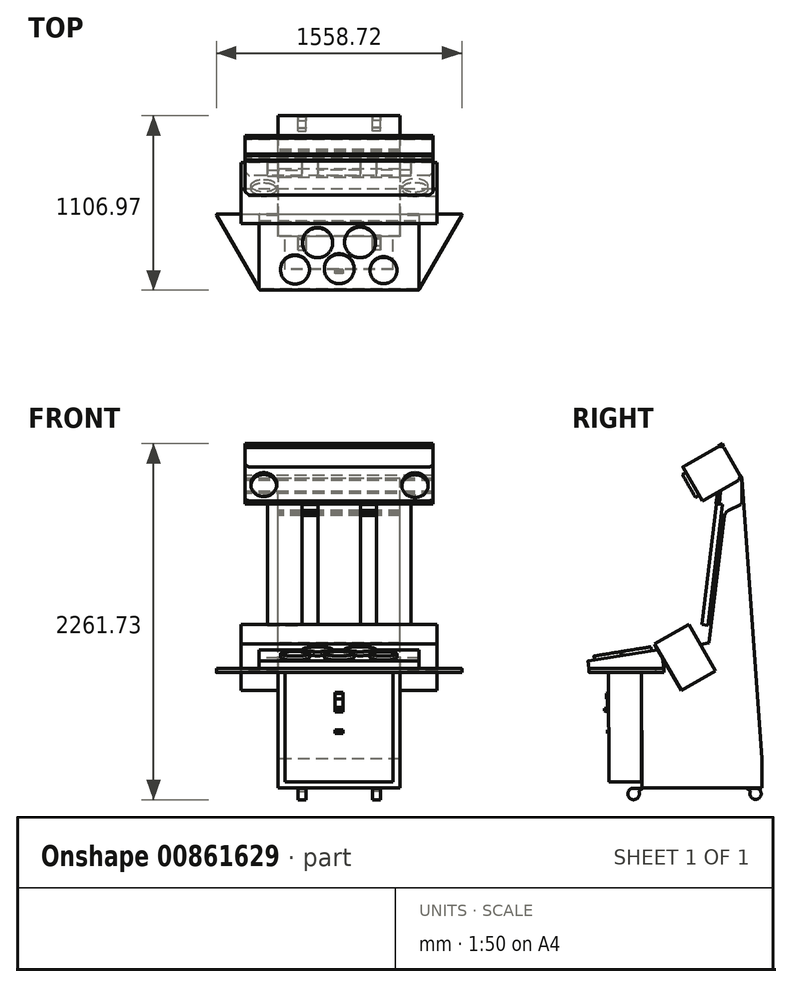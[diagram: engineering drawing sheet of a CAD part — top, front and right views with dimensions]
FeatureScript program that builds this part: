
annotation { "Feature Type Name" : "Feature", "Feature Type Description" : "" }
export const myFeature = defineFeature(function(context is Context, id is Id, definition is map)
    precondition{}
    {
        {
            var Q0;
            Q0=qCreatedBy(makeId("Right.planeOp"),FACE);
            cPlane(context, id + "F0", {"entities" : qUnion([Q0]), "cplaneType" : CPlaneType.OFFSET, "offset" : 210 * mm, "width" : 152.4 * mm, "height" : 152.4 * mm});
        }
        {
            var Q0;
            Q0=qCreatedBy(makeId("Right.planeOp"),FACE);
            var sketch = newSketch(context, id + "F1", { "sketchPlane" : qUnion([Q0])});
            skLineSegment(sketch, "E0", {"start": v(135.82, -1032.26) * mm, "end": v(135.82, 1003.74) * mm});
            skLineSegment(sketch, "E1", {"start": v(-110.75, -958.44) * mm, "end": v(-873.39, -958.44) * mm});
            skLineSegment(sketch, "E2", {"start": v(-873.39, -931.24) * mm, "end": v(-111.51, -931.24) * mm});
            skLineSegment(sketch, "E3", {"start": v(-110.75, -958.44) * mm, "end": v(-110.75, -776.07) * mm});
            skLineSegment(sketch, "E4", {"start": v(-110.75, -776.07) * mm, "end": v(-237.96, 1006.21) * mm});
            skLineSegment(sketch, "E5", {"start": v(-873.39, -958.44) * mm, "end": v(-877.45, -225.16) * mm});
            skLineSegment(sketch, "E6", {"start": v(-877.45, -225.16) * mm, "end": v(-784.62, -224.64) * mm});
            skLineSegment(sketch, "E7", {"start": v(-784.62, -224.64) * mm, "end": v(-803.14, -88.35) * mm});
            skLineSegment(sketch, "E8", {"start": v(-803.14, -88.35) * mm, "end": v(-449.35, -40.28) * mm});
            skLineSegment(sketch, "E9", {"start": v(-449.35, -40.28) * mm, "end": v(-351.09, 769.66) * mm});
            skLineSegment(sketch, "E10", {"start": v(-351.09, 769.66) * mm, "end": v(-345.66, 781.97) * mm});
            skLineSegment(sketch, "E11", {"start": v(-345.66, 781.97) * mm, "end": v(-337.87, 793.88) * mm});
            skLineSegment(sketch, "E12", {"start": v(-337.87, 793.88) * mm, "end": v(-325.04, 803.04) * mm});
            skLineSegment(sketch, "E13", {"start": v(-325.04, 803.04) * mm, "end": v(-246.25, 841.07) * mm});
            skLineSegment(sketch, "E14", {"start": v(-246.25, 841.07) * mm, "end": v(-242.89, 847.1) * mm});
            skLineSegment(sketch, "E15", {"start": v(-242.89, 847.1) * mm, "end": v(-239.22, 854.43) * mm});
            skLineSegment(sketch, "E16", {"start": v(-239.22, 854.43) * mm, "end": v(-237.96, 1006.21) * mm});
            skSolve(sketch);
        }
        {
            var Q0;
            Q0=makeQuery(id+"F1.imprint","IMPRINT",FACE,{"disambiguationData":[TD([[makeQuery(id+"F1.imprint","IMPRINT",EDGE,{"derivedFrom":sQuery(id+"F1.wireOp",EDGE,"E1")}),-1.0]])]});
            extrude(context, id + "F2", {"entities" : qUnion([Q0]), "depth" : 774.7 * mm, "offsetDistance" : 25.4 * mm, "symmetric" : true});
        }
        {
            var Q0;
            Q0=qCreatedBy(makeId("Right.planeOp"),FACE);
            var sketch = newSketch(context, id + "F3", { "sketchPlane" : qUnion([Q0])});
            skLineSegment(sketch, "E17", {"start": v(-615.4, 1079.1) * mm, "end": v(-490.16, 861.86) * mm});
            skLineSegment(sketch, "E18", {"start": v(-490.16, 861.86) * mm, "end": v(-262.73, 992.99) * mm});
            skLineSegment(sketch, "E19", {"start": v(-262.73, 992.99) * mm, "end": v(-255.5, 1005.4) * mm});
            skLineSegment(sketch, "E20", {"start": v(-255.5, 1005.4) * mm, "end": v(-252.31, 1026.09) * mm});
            skLineSegment(sketch, "E21", {"start": v(-252.31, 1026.09) * mm, "end": v(-354.74, 1202.65) * mm});
            skLineSegment(sketch, "E22", {"start": v(-354.74, 1202.65) * mm, "end": v(-367.56, 1207.47) * mm});
            skLineSegment(sketch, "E23", {"start": v(-367.56, 1207.47) * mm, "end": v(-382.08, 1207.47) * mm});
            skLineSegment(sketch, "E24", {"start": v(-382.08, 1207.47) * mm, "end": v(-396.8, 1202.65) * mm});
            skLineSegment(sketch, "E25", {"start": v(-396.8, 1202.65) * mm, "end": v(-615.4, 1079.1) * mm});
            skLineSegment(sketch, "E26", {"start": v(-538.42, 1122.61) * mm, "end": v(-413.55, 906.03) * mm});
            skSolve(sketch);
        }
        {
            var Q0;
            Q0 = qSketchRegion(id + "F3", true);
            extrude(context, id + "F4", {"entities" : qUnion([Q0]), "depth" : 1193.8 * mm, "offsetDistance" : 25.4 * mm, "symmetric" : true});
        }
        {
            var Q0;
            Q0=qCreatedBy(makeId("Right.planeOp"),FACE);
            var sketch = newSketch(context, id + "F5", { "sketchPlane" : qUnion([Q0])});
            skLineSegment(sketch, "E27", {"start": v(-795.55, -46.75) * mm, "end": v(-576.34, 79.37) * mm});
            skLineSegment(sketch, "E28", {"start": v(-576.34, 79.37) * mm, "end": v(-406.78, -215.33) * mm});
            skLineSegment(sketch, "E29", {"start": v(-406.78, -215.33) * mm, "end": v(-624.22, -340.43) * mm});
            skLineSegment(sketch, "E30", {"start": v(-624.22, -340.43) * mm, "end": v(-795.55, -46.75) * mm});
            skLineSegment(sketch, "E31", {"start": v(-749.98, -124.87) * mm, "end": v(-532, 2.3) * mm});
            skSolve(sketch);
        }
        {
            var Q0;
            Q0 = qSketchRegion(id + "F5", true);
            extrude(context, id + "F6", {"entities" : qUnion([Q0]), "operationType" : NewBodyOperationType.ADD, "depth" : 1244.6 * mm, "offsetDistance" : 25.4 * mm, "symmetric" : true});
        }
        {
            var Q0;
            Q0=qCreatedBy(makeId("Right.planeOp"),FACE);
            var sketch = newSketch(context, id + "F7", { "sketchPlane" : qUnion([Q0])});
            skLineSegment(sketch, "E32", {"start": v(-1223.23, -201.66) * mm, "end": v(-733.46, -201.66) * mm});
            skLineSegment(sketch, "E33", {"start": v(-733.46, -201.66) * mm, "end": v(-753.47, -78.71) * mm});
            skLineSegment(sketch, "E34", {"start": v(-753.47, -78.71) * mm, "end": v(-1229.15, -156.15) * mm});
            skLineSegment(sketch, "E35", {"start": v(-1217.72, -154.29) * mm, "end": v(-1210, -201.66) * mm});
            skLineSegment(sketch, "E36", {"start": v(-1141.93, -141.95) * mm, "end": v(-1132.2, -201.66) * mm});
            skSolve(sketch);
        }
        {
            var Q0;
            Q0 = qSketchRegion(id + "F7", true);
            extrude(context, id + "F8", {"entities" : qUnion([Q0]), "operationType" : NewBodyOperationType.ADD, "depth" : 1016 * mm, "offsetDistance" : 25.4 * mm, "symmetric" : true});
        }
        {
            var Q0;
            Q0=qCreatedBy(makeId("Right.planeOp"),FACE);
            var sketch = newSketch(context, id + "F9", { "sketchPlane" : qUnion([Q0])});
            skLineSegment(sketch, "E37", {"start": v(-977.2, -301.46) * mm, "end": v(-901, -301.46) * mm});
            skLineSegment(sketch, "E38", {"start": v(-977.2, -301.46) * mm, "end": v(-977.2, -851.46) * mm});
            skLineSegment(sketch, "E39", {"start": v(-977.2, -851.46) * mm, "end": v(-901.79, -851.46) * mm});
            skLineSegment(sketch, "E40", {"start": v(-901.79, -851.46) * mm, "end": v(-901, -301.46) * mm});
            skSolve(sketch);
        }
        {
            var Q0;
            Q0 = qSketchRegion(id + "F9", true);
            extrude(context, id + "F10", {"entities" : qUnion([Q0]), "depth" : 533.4 * mm, "offsetDistance" : 25.4 * mm, "symmetric" : true});
        }
        {
            var Q0;
            Q0=makeQuery(id+"F8.opExtrude","SWEPT_FACE",FACE,{"disambiguationData":[OSD([sQuery(id+"F7.wireOp",EDGE,"E34")])]});
            var sketch = newSketch(context, id + "F11", { "sketchPlane" : qUnion([Q0])});
            skCircle(sketch, "E41", {"center": v(-137.58, -918.6) * mm, "radius": 95.8 * mm});
            skCircle(sketch, "E42", {"center": v(132.62, -915.7) * mm, "radius": 98.49 * mm});
            skCircle(sketch, "E43", {"center": v(-280.8, -1092.1) * mm, "radius": 91.63 * mm});
            skCircle(sketch, "E44", {"center": v(281.26, -1096.57) * mm, "radius": 85.14 * mm});
            skCircle(sketch, "E45", {"center": v(0, -1086.83) * mm, "radius": 94.68 * mm});
            skSolve(sketch);
        }
        {
            var Q0;
            Q0 = qSketchRegion(id + "F11", true);
            extrude(context, id + "F12", {"entities" : qUnion([Q0]), "operationType" : NewBodyOperationType.ADD, "depth" : 50.8 * mm, "offsetDistance" : 25.4 * mm, "symmetric" : true});
        }
        {
            var Q0;
            Q0=qCreatedBy(id+"F0.planeOp",FACE);
            var sketch = newSketch(context, id + "F13", { "sketchPlane" : qUnion([Q0])});
            skLineSegment(sketch, "E46", {"start": v(-207.52, -962.58) * mm, "end": v(-154.05, -1009.27) * mm});
            skLineSegment(sketch, "E47", {"start": v(-207.52, -962.58) * mm, "end": v(-142.16, -962.58) * mm});
            skLineSegment(sketch, "E48", {"start": v(-142.16, -962.58) * mm, "end": v(-136.22, -992.3) * mm});
            skLineSegment(sketch, "E49", {"start": v(-136.22, -992.3) * mm, "end": v(-138.79, -1001.43) * mm});
            skLineSegment(sketch, "E50", {"start": v(-138.79, -1001.43) * mm, "end": v(-142.78, -1006) * mm});
            skLineSegment(sketch, "E51", {"start": v(-142.78, -1006) * mm, "end": v(-154.05, -1009.27) * mm});
            skArc(sketch, "E52", {"start": v(-185.18, -982.09) * mm, "mid": v(-137.8, -1029.41) * mm, "end": v(-142.16, -962.58) * mm});
            skLineSegment(sketch, "E53", {"start": v(-871.96, -962.48) * mm, "end": v(-937.74, -962.48) * mm});
            skLineSegment(sketch, "E54", {"start": v(-937.74, -962.48) * mm, "end": v(-945.38, -989.64) * mm});
            skLineSegment(sketch, "E55", {"start": v(-945.38, -989.64) * mm, "end": v(-944.06, -1001.7) * mm});
            skLineSegment(sketch, "E56", {"start": v(-944.06, -1001.7) * mm, "end": v(-936.38, -1007.05) * mm});
            skLineSegment(sketch, "E57", {"start": v(-936.38, -1007.05) * mm, "end": v(-924.96, -1007.05) * mm});
            skLineSegment(sketch, "E58", {"start": v(-924.96, -1007.05) * mm, "end": v(-871.96, -962.48) * mm});
            skArc(sketch, "E59", {"start": v(-937.74, -962.48) * mm, "mid": v(-941.48, -1031.6) * mm, "end": v(-894.12, -981.11) * mm});
            skSolve(sketch);
        }
        {
            var Q0;
            Q0 = qSketchRegion(id + "F13", true);
            extrude(context, id + "F14", {"entities" : qUnion([Q0]), "depth" : 50.8 * mm, "offsetDistance" : 25.4 * mm});
        }
        {
            var Q0;
            Q0=qCreatedBy(makeId("Right.planeOp"),FACE);
            var sketch = newSketch(context, id + "F15", { "sketchPlane" : qUnion([Q0])});
            skLineSegment(sketch, "E60", {"start": v(-362.5, 840.95) * mm, "end": v(-401.41, 843.95) * mm});
            skLineSegment(sketch, "E61", {"start": v(-401.41, 843.95) * mm, "end": v(-493.98, 77.86) * mm});
            skLineSegment(sketch, "E62", {"start": v(-493.98, 77.86) * mm, "end": v(-454.6, 73.1) * mm});
            skLineSegment(sketch, "E63", {"start": v(-454.6, 73.1) * mm, "end": v(-362.5, 840.95) * mm});
            skSolve(sketch);
        }
        {
            var Q0;
            Q0 = qSketchRegion(id + "F15", true);
            extrude(context, id + "F16", {"entities" : qUnion([Q0]), "depth" : 270 * mm, "offsetDistance" : 25.4 * mm, "symmetric" : true});
        }
        {
            var Q0;
            Q0=qCreatedBy(makeId("Right.planeOp"),FACE);
            var sketch = newSketch(context, id + "F17", { "sketchPlane" : qUnion([Q0])});
            skLineSegment(sketch, "E64", {"start": v(-255.02, 994.86) * mm, "end": v(-236.35, 1006.75) * mm});
            skLineSegment(sketch, "E65", {"start": v(-255.02, 994.86) * mm, "end": v(-249.98, 1026.27) * mm});
            skLineSegment(sketch, "E66", {"start": v(-249.98, 1026.27) * mm, "end": v(-236.35, 1006.75) * mm});
            skLineSegment(sketch, "E67", {"start": v(-364.5, 1227.17) * mm, "end": v(-391.26, 1211.27) * mm});
            skLineSegment(sketch, "E68", {"start": v(-391.26, 1211.27) * mm, "end": v(-355.17, 1209) * mm});
            skLineSegment(sketch, "E69", {"start": v(-355.17, 1209) * mm, "end": v(-364.5, 1227.17) * mm});
            skLineSegment(sketch, "E70", {"start": v(-403.29, 847.41) * mm, "end": v(-395.65, 911.5) * mm});
            skLineSegment(sketch, "E71", {"start": v(-395.65, 911.5) * mm, "end": v(-375.7, 924.23) * mm});
            skLineSegment(sketch, "E72", {"start": v(-403.29, 847.41) * mm, "end": v(-362.3, 842.52) * mm});
            skLineSegment(sketch, "E73", {"start": v(-375.7, 924.23) * mm, "end": v(-382.8, 844.97) * mm});
            skLineSegment(sketch, "E74", {"start": v(-373.82, 743.38) * mm, "end": v(-375.43, 737.85) * mm});
            skLineSegment(sketch, "E75", {"start": v(-375.43, 737.85) * mm, "end": v(-355.09, 737.85) * mm});
            skLineSegment(sketch, "E76", {"start": v(-355.09, 737.85) * mm, "end": v(-355.09, 741.95) * mm});
            skLineSegment(sketch, "E77", {"start": v(-355.09, 741.95) * mm, "end": v(-373.82, 743.38) * mm});
            skLineSegment(sketch, "E78", {"start": v(-388.1, 623.82) * mm, "end": v(-369, 622.22) * mm});
            skLineSegment(sketch, "E79", {"start": v(-369, 622.22) * mm, "end": v(-369.41, 617.36) * mm});
            skLineSegment(sketch, "E80", {"start": v(-369.41, 617.36) * mm, "end": v(-388.83, 619) * mm});
            skLineSegment(sketch, "E81", {"start": v(-388.83, 619) * mm, "end": v(-388.1, 623.82) * mm});
            skLineSegment(sketch, "E82", {"start": v(-405.23, 483.75) * mm, "end": v(-386.14, 483.75) * mm});
            skLineSegment(sketch, "E83", {"start": v(-386.14, 483.75) * mm, "end": v(-386.65, 477.65) * mm});
            skLineSegment(sketch, "E84", {"start": v(-386.65, 477.65) * mm, "end": v(-405.81, 479.26) * mm});
            skLineSegment(sketch, "E85", {"start": v(-405.81, 479.26) * mm, "end": v(-405.23, 483.75) * mm});
            skLineSegment(sketch, "E86", {"start": v(-418.61, 367.58) * mm, "end": v(-419.1, 361.76) * mm});
            skLineSegment(sketch, "E87", {"start": v(-419.1, 361.76) * mm, "end": v(-400.77, 361.76) * mm});
            skLineSegment(sketch, "E88", {"start": v(-400.77, 361.76) * mm, "end": v(-400.27, 367.64) * mm});
            skLineSegment(sketch, "E89", {"start": v(-400.27, 367.64) * mm, "end": v(-418.61, 367.58) * mm});
            skLineSegment(sketch, "E90", {"start": v(-431.82, 257.66) * mm, "end": v(-431.82, 254.45) * mm});
            skLineSegment(sketch, "E91", {"start": v(-431.82, 254.45) * mm, "end": v(-413.8, 254.45) * mm});
            skLineSegment(sketch, "E92", {"start": v(-413.8, 254.45) * mm, "end": v(-413.8, 257.3) * mm});
            skLineSegment(sketch, "E93", {"start": v(-413.8, 257.3) * mm, "end": v(-431.82, 257.66) * mm});
            skLineSegment(sketch, "E94", {"start": v(-445.56, 141.14) * mm, "end": v(-446.23, 133.18) * mm});
            skLineSegment(sketch, "E95", {"start": v(-446.23, 133.18) * mm, "end": v(-428.6, 134.71) * mm});
            skLineSegment(sketch, "E96", {"start": v(-428.6, 134.71) * mm, "end": v(-428.04, 141.39) * mm});
            skLineSegment(sketch, "E97", {"start": v(-428.04, 141.39) * mm, "end": v(-445.56, 141.14) * mm});
            skLineSegment(sketch, "E98", {"start": v(-457.65, 70.28) * mm, "end": v(-498.53, 73.72) * mm});
            skLineSegment(sketch, "E99", {"start": v(-498.53, 73.72) * mm, "end": v(-503.38, 15.97) * mm});
            skLineSegment(sketch, "E100", {"start": v(-503.38, 15.97) * mm, "end": v(-488.26, -14.95) * mm});
            skLineSegment(sketch, "E101", {"start": v(-488.26, -14.95) * mm, "end": v(-447.73, -18.36) * mm});
            skLineSegment(sketch, "E102", {"start": v(-447.73, -18.36) * mm, "end": v(-436.04, 68.48) * mm});
            skLineSegment(sketch, "E103", {"start": v(-488.26, -14.95) * mm, "end": v(-480.93, 72.24) * mm});
            skSolve(sketch);
        }
        {
            var Q0;
            Q0=makeQuery(id+"F17.imprint","IMPRINT",FACE,{"disambiguationData":[TD([[makeQuery(id+"F17.imprint","IMPRINT",EDGE,{"derivedFrom":sQuery(id+"F17.wireOp",EDGE,"E64")}),1.0]])]});
            var Q1;
            Q1=makeQuery(id+"F17.imprint","IMPRINT",FACE,{"disambiguationData":[TD([[makeQuery(id+"F17.imprint","IMPRINT",EDGE,{"derivedFrom":sQuery(id+"F17.wireOp",EDGE,"E67")}),1.0]])]});
            var Q2;
            {var subQ0=sQuery(id+"F17.wireOp",EDGE,"E70");Q2=makeQuery(id+"F17.imprint","IMPRINT",FACE,{"disambiguationData":[TD([[makeQuery(id+"F17.imprint","IMPRINT",EDGE,{"derivedFrom":subQ0}),-1.0]])]});}
            extrude(context, id + "F18", {"entities" : qUnion([Q0, Q1, Q2]), "operationType" : NewBodyOperationType.ADD, "depth" : 1193.8 * mm, "offsetDistance" : 25.4 * mm, "symmetric" : true});
        }
        {
            var Q0;
            Q0=makeQuery(id+"F16.opExtrude","CAP_FACE",FACE,{"disambiguationData":[OSD([sQuery(id+"F15.wireOp",EDGE,"E60"),sQuery(id+"F15.wireOp",EDGE,"E61"),sQuery(id+"F15.wireOp",EDGE,"E62"),sQuery(id+"F15.wireOp",EDGE,"E63")])],"isStart":false});
            var sketch = newSketch(context, id + "F19", { "sketchPlane" : qUnion([Q0])});
            skLineSegment(sketch, "E104", {"start": v(-362.5, 840.95) * mm, "end": v(-401.41, 843.95) * mm});
            skLineSegment(sketch, "E105", {"start": v(-401.41, 843.95) * mm, "end": v(-493.98, 77.86) * mm});
            skLineSegment(sketch, "E106", {"start": v(-493.98, 77.86) * mm, "end": v(-454.6, 73.1) * mm});
            skLineSegment(sketch, "E107", {"start": v(-454.6, 73.1) * mm, "end": v(-362.5, 840.95) * mm});
            skSolve(sketch);
        }
        {
            var Q0;
            Q0=makeQuery(id+"F19.imprint","IMPRINT",FACE,{"disambiguationData":[TD([[makeQuery(id+"F19.imprint","IMPRINT",EDGE,{"derivedFrom":sQuery(id+"F19.wireOp",EDGE,"E104")}),1.0]])]});
            extrude(context, id + "F20", {"entities" : qUnion([Q0]), "depth" : 218.44 * mm, "offsetDistance" : 25.4 * mm});
        }
        {
            var Q0;
            Q0=makeQuery(id+"F16.opExtrude","CAP_FACE",FACE,{"disambiguationData":[OSD([sQuery(id+"F15.wireOp",EDGE,"E60"),sQuery(id+"F15.wireOp",EDGE,"E61"),sQuery(id+"F15.wireOp",EDGE,"E62"),sQuery(id+"F15.wireOp",EDGE,"E63")])],"isStart":true});
            var sketch = newSketch(context, id + "F21", { "sketchPlane" : qUnion([Q0])});
            skLineSegment(sketch, "E108", {"start": v(362.5, 840.95) * mm, "end": v(401.41, 843.95) * mm});
            skLineSegment(sketch, "E109", {"start": v(401.41, 843.95) * mm, "end": v(493.98, 77.86) * mm});
            skLineSegment(sketch, "E110", {"start": v(493.98, 77.86) * mm, "end": v(454.6, 73.1) * mm});
            skLineSegment(sketch, "E111", {"start": v(454.6, 73.1) * mm, "end": v(362.5, 840.95) * mm});
            skLineSegment(sketch, "E112", {"start": v(-1523.89, 16566.5) * mm, "end": v(-1498.67, 16569.52) * mm, "construction": true});
            skSolve(sketch);
        }
        {
            var Q0;
            Q0=makeQuery(id+"F21.imprint","IMPRINT",FACE,{"disambiguationData":[TD([[makeQuery(id+"F21.imprint","IMPRINT",EDGE,{"derivedFrom":sQuery(id+"F21.wireOp",EDGE,"E108")}),-1.0]])]});
            extrude(context, id + "F22", {"entities" : qUnion([Q0]), "depth" : 218.44 * mm, "offsetDistance" : 25.4 * mm});
        }
        {
            var Q0;
            Q0=makeQuery(id+"F4.opExtrude","SWEPT_FACE",FACE,{"disambiguationData":[OSD([sQuery(id+"F3.wireOp",EDGE,"E17")])]});
            var sketch = newSketch(context, id + "F23", { "sketchPlane" : qUnion([Q0])});
            skCircle(sketch, "E113", {"center": v(-479.44, 1120.03) * mm, "radius": 80.75 * mm});
            skCircle(sketch, "E114", {"center": v(481.49, 1116.55) * mm, "radius": 83.14 * mm});
            skSolve(sketch);
        }
        {
            var Q0;
            Q0 = qSketchRegion(id + "F23", true);
            extrude(context, id + "F24", {"entities" : qUnion([Q0]), "operationType" : NewBodyOperationType.ADD, "depth" : 25.4 * mm, "offsetDistance" : 25.4 * mm});
        }
        {
            var Q0;
            Q0=qCreatedBy(makeId("Right.planeOp"),FACE);
            var sketch = newSketch(context, id + "F25", { "sketchPlane" : qUnion([Q0])});
            skLineSegment(sketch, "E115", {"start": v(-1086.29, -225.42) * mm, "end": v(-878.87, -225.42) * mm});
            skLineSegment(sketch, "E116", {"start": v(-1085.43, -922.56) * mm, "end": v(-876.26, -922.56) * mm});
            skLineSegment(sketch, "E117", {"start": v(-1086.29, -225.42) * mm, "end": v(-1085.43, -922.56) * mm});
            skLineSegment(sketch, "E118", {"start": v(-876.26, -922.56) * mm, "end": v(-878.87, -225.42) * mm});
            skSolve(sketch);
        }
        {
            var Q0;
            Q0=makeQuery(id+"F25.imprint","IMPRINT",FACE,{"disambiguationData":[TD([[makeQuery(id+"F25.imprint","IMPRINT",EDGE,{"derivedFrom":sQuery(id+"F25.wireOp",EDGE,"E115")}),-1.0]])]});
            extrude(context, id + "F26", {"entities" : qUnion([Q0]), "operationType" : NewBodyOperationType.ADD, "depth" : 685.8 * mm, "offsetDistance" : 25.4 * mm, "symmetric" : true});
        }
        {
            var Q0;
            Q0=qCreatedBy(makeId("Right.planeOp"),FACE);
            var sketch = newSketch(context, id + "F27", { "sketchPlane" : qUnion([Q0])});
            skLineSegment(sketch, "E119", {"start": v(-1086.45, -352.21) * mm, "end": v(-1086.45, -475.86) * mm});
            skLineSegment(sketch, "E120", {"start": v(-1086.45, -475.86) * mm, "end": v(-1094.85, -475.86) * mm});
            skLineSegment(sketch, "E121", {"start": v(-1094.85, -475.86) * mm, "end": v(-1111.66, -470.45) * mm});
            skLineSegment(sketch, "E122", {"start": v(-1111.66, -470.45) * mm, "end": v(-1111.66, -454.85) * mm});
            skLineSegment(sketch, "E123", {"start": v(-1111.66, -454.85) * mm, "end": v(-1098.45, -454.85) * mm});
            skLineSegment(sketch, "E124", {"start": v(-1098.45, -454.85) * mm, "end": v(-1093.65, -448.25) * mm});
            skLineSegment(sketch, "E125", {"start": v(-1093.65, -448.25) * mm, "end": v(-1093.65, -395.43) * mm});
            skLineSegment(sketch, "E126", {"start": v(-1093.65, -395.43) * mm, "end": v(-1100.25, -395.43) * mm});
            skLineSegment(sketch, "E127", {"start": v(-1100.25, -395.43) * mm, "end": v(-1100.25, -358.22) * mm});
            skLineSegment(sketch, "E128", {"start": v(-1100.25, -358.22) * mm, "end": v(-1086.45, -352.21) * mm});
            skLineSegment(sketch, "E129", {"start": v(-1086.45, -593.5) * mm, "end": v(-1086.45, -613.3) * mm});
            skLineSegment(sketch, "E130", {"start": v(-1086.45, -613.3) * mm, "end": v(-1093.05, -613.3) * mm});
            skLineSegment(sketch, "E131", {"start": v(-1093.05, -613.3) * mm, "end": v(-1093.05, -592.9) * mm});
            skLineSegment(sketch, "E132", {"start": v(-1093.05, -592.9) * mm, "end": v(-1086.45, -593.5) * mm});
            skSolve(sketch);
        }
        {
            var Q0;
            Q0 = qSketchRegion(id + "F27", true);
            extrude(context, id + "F28", {"entities" : qUnion([Q0]), "depth" : 50.8 * mm, "offsetDistance" : 25.4 * mm, "symmetric" : true});
        }
        {
            var Q0;
            Q0=makeQuery(id+"F14.opExtrude","SWEPT_BODY",BODY,{"disambiguationData":[OSD([sQuery(id+"F13.wireOp",EDGE,"E46"),sQuery(id+"F13.wireOp",EDGE,"E47"),sQuery(id+"F13.wireOp",EDGE,"E52")])]});
            var Q1;
            Q1=makeQuery(id+"F14.opExtrude","SWEPT_BODY",BODY,{"disambiguationData":[OSD([sQuery(id+"F13.wireOp",EDGE,"E53"),sQuery(id+"F13.wireOp",EDGE,"E58"),sQuery(id+"F13.wireOp",EDGE,"E59")])]});
            var Q2;
            Q2=qCreatedBy(makeId("Right.planeOp"),FACE);
            mirror(context, id + "F29", {"entities" : qUnion([Q0, Q1]), "mirrorPlane" : qUnion([Q2])});
        }
        {
            var Q0;
            Q0=makeQuery(id+"F8.opExtrude","SWEPT_FACE",FACE,{"disambiguationData":[OSD([sQuery(id+"F7.wireOp",EDGE,"E32")])]});
            var sketch = newSketch(context, id + "F30", { "sketchPlane" : qUnion([Q0])});
            skLineSegment(sketch, "E133", {"start": v(-783.07, 733.46) * mm, "end": v(783.07, 733.46) * mm});
            skLineSegment(sketch, "E134", {"start": v(783.07, 733.46) * mm, "end": v(508, 1210) * mm});
            skLineSegment(sketch, "E135", {"start": v(508, 1210) * mm, "end": v(-508, 1210) * mm});
            skLineSegment(sketch, "E136", {"start": v(-508, 1210) * mm, "end": v(-783.07, 733.46) * mm});
            skSolve(sketch);
        }
        {
            var Q0;
            Q0 = qSketchRegion(id + "F30", true);
            extrude(context, id + "F31", {"entities" : qUnion([Q0]), "depth" : 25.4 * mm, "offsetDistance" : 25.4 * mm});
        }
        {
            var Q0;
            Q0=makeQuery(id+"F31.opExtrude","SWEPT_EDGE",EDGE,{"disambiguationData":[OSD([sQuery(id+"F30.wireOp",EDGE,"E133"),sQuery(id+"F30.wireOp",EDGE,"E134")])]});
            var Q1;
            Q1=makeQuery(id+"F31.opExtrude","SWEPT_EDGE",EDGE,{"disambiguationData":[OSD([sQuery(id+"F7.wireOp",EDGE,"E32"),sQuery(id+"F30.wireOp",EDGE,"E134"),sQuery(id+"F30.wireOp",EDGE,"E135")])]});
            var Q2;
            Q2=makeQuery(id+"F8.opExtrude","CAP_EDGE",EDGE,{"disambiguationData":[OSD([sQuery(id+"F7.wireOp",EDGE,"E35")])],"isStart":false});
            var Q3;
            Q3=makeQuery(id+"F8.opExtrude","CAP_EDGE",EDGE,{"disambiguationData":[OSD([sQuery(id+"F7.wireOp",EDGE,"E35")])],"isStart":true});
            var Q4;
            Q4=makeQuery(id+"F31.opExtrude","SWEPT_EDGE",EDGE,{"disambiguationData":[OSD([sQuery(id+"F7.wireOp",EDGE,"E32"),sQuery(id+"F30.wireOp",EDGE,"E135"),sQuery(id+"F30.wireOp",EDGE,"E136")])]});
            var Q5;
            Q5=makeQuery(id+"F31.opExtrude","SWEPT_EDGE",EDGE,{"disambiguationData":[OSD([sQuery(id+"F30.wireOp",EDGE,"E133"),sQuery(id+"F30.wireOp",EDGE,"E136")])]});
            fillet(context, id + "F32", {"entities" : qUnion([Q0, Q1, Q2, Q3, Q4, Q5]), "radius" : 5.08 * mm, "tangentPropagation" : true, "allowEdgeOverflow" : false});
        }
        {
            var Q0;
            Q0=makeQuery(id+"F4.opExtrude","CAP_EDGE",EDGE,{"disambiguationData":[OSD([sQuery(id+"F3.wireOp",EDGE,"E17")])],"isStart":false});
            var Q1;
            Q1=makeQuery(id+"F4.opExtrude","CAP_EDGE",EDGE,{"disambiguationData":[OSD([sQuery(id+"F3.wireOp",EDGE,"E17")])],"isStart":true});
            chamfer(context, id + "F33", {"entities" : qUnion([Q0, Q1]), "width" : 25.4 * mm, "tangentPropagation" : true});
        }
        {
            var Q0;
            {var subQ0=sQuery(id+"F3.wireOp",EDGE,"E17");Q0=makeQuery(id+"F33.opChamfer","BLEND_EDGE",EDGE,{"blendedFrom":[makeQuery(id+"F4.opExtrude","CAP_EDGE",EDGE,{"disambiguationData":[OSD([subQ0])],"isStart":false}),makeQuery(id+"F4.opExtrude","CAP_FACE",FACE,{"disambiguationData":[OSD([subQ0,sQuery(id+"F3.wireOp",EDGE,"E18"),sQuery(id+"F3.wireOp",EDGE,"E19"),sQuery(id+"F3.wireOp",EDGE,"E20"),sQuery(id+"F3.wireOp",EDGE,"E21"),sQuery(id+"F3.wireOp",EDGE,"E22"),sQuery(id+"F3.wireOp",EDGE,"E23"),sQuery(id+"F3.wireOp",EDGE,"E24"),sQuery(id+"F3.wireOp",EDGE,"E25")])],"isStart":false})],"blendedInto":[makeQuery(id+"F4.opExtrude","CAP_FACE",FACE,{"disambiguationData":[OSD([subQ0,sQuery(id+"F3.wireOp",EDGE,"E18"),sQuery(id+"F3.wireOp",EDGE,"E19"),sQuery(id+"F3.wireOp",EDGE,"E20"),sQuery(id+"F3.wireOp",EDGE,"E21"),sQuery(id+"F3.wireOp",EDGE,"E22"),sQuery(id+"F3.wireOp",EDGE,"E23"),sQuery(id+"F3.wireOp",EDGE,"E24"),sQuery(id+"F3.wireOp",EDGE,"E25")])],"isStart":false})]});}
            var Q1;
            {var subQ0=sQuery(id+"F3.wireOp",EDGE,"E17");Q1=makeQuery(id+"F33.opChamfer","BLEND_EDGE",EDGE,{"blendedFrom":[makeQuery(id+"F4.opExtrude","CAP_EDGE",EDGE,{"disambiguationData":[OSD([subQ0])],"isStart":false}),makeQuery(id+"F4.opExtrude","SWEPT_FACE",FACE,{"disambiguationData":[OSD([subQ0])]})],"blendedInto":[makeQuery(id+"F4.opExtrude","SWEPT_FACE",FACE,{"disambiguationData":[OSD([subQ0])]})]});}
            var Q2;
            {var subQ0=sQuery(id+"F3.wireOp",EDGE,"E17");Q2=makeQuery(id+"F33.opChamfer","BLEND_EDGE",EDGE,{"blendedFrom":[makeQuery(id+"F4.opExtrude","CAP_EDGE",EDGE,{"disambiguationData":[OSD([subQ0])],"isStart":true}),makeQuery(id+"F4.opExtrude","SWEPT_FACE",FACE,{"disambiguationData":[OSD([subQ0])]})],"blendedInto":[makeQuery(id+"F4.opExtrude","SWEPT_FACE",FACE,{"disambiguationData":[OSD([subQ0])]})]});}
            var Q3;
            {var subQ0=sQuery(id+"F3.wireOp",EDGE,"E17");Q3=makeQuery(id+"F33.opChamfer","BLEND_EDGE",EDGE,{"blendedFrom":[makeQuery(id+"F4.opExtrude","CAP_EDGE",EDGE,{"disambiguationData":[OSD([subQ0])],"isStart":true}),makeQuery(id+"F4.opExtrude","CAP_FACE",FACE,{"disambiguationData":[OSD([subQ0,sQuery(id+"F3.wireOp",EDGE,"E18"),sQuery(id+"F3.wireOp",EDGE,"E19"),sQuery(id+"F3.wireOp",EDGE,"E20"),sQuery(id+"F3.wireOp",EDGE,"E21"),sQuery(id+"F3.wireOp",EDGE,"E22"),sQuery(id+"F3.wireOp",EDGE,"E23"),sQuery(id+"F3.wireOp",EDGE,"E24"),sQuery(id+"F3.wireOp",EDGE,"E25")])],"isStart":true})],"blendedInto":[makeQuery(id+"F4.opExtrude","CAP_FACE",FACE,{"disambiguationData":[OSD([subQ0,sQuery(id+"F3.wireOp",EDGE,"E18"),sQuery(id+"F3.wireOp",EDGE,"E19"),sQuery(id+"F3.wireOp",EDGE,"E20"),sQuery(id+"F3.wireOp",EDGE,"E21"),sQuery(id+"F3.wireOp",EDGE,"E22"),sQuery(id+"F3.wireOp",EDGE,"E23"),sQuery(id+"F3.wireOp",EDGE,"E24"),sQuery(id+"F3.wireOp",EDGE,"E25")])],"isStart":true})]});}
            fillet(context, id + "F34", {"entities" : qUnion([Q0, Q1, Q2, Q3]), "radius" : 5.08 * mm, "tangentPropagation" : true, "allowEdgeOverflow" : false});
        }
        {
            var Q0;
            Q0=makeQuery(id+"F22.opExtrude","SWEPT_BODY",BODY,{"disambiguationData":[OSD([sQuery(id+"F21.wireOp",EDGE,"E108"),sQuery(id+"F21.wireOp",EDGE,"E109"),sQuery(id+"F21.wireOp",EDGE,"E110"),sQuery(id+"F21.wireOp",EDGE,"E111")])]});
            transform(context, id + "F35", {"entities" : qUnion([Q0]), "transformType" : TransformType.TRANSLATION_3D, "dx" : -101.6 * mm, "dy" : 0 * mm, "dz" : 0 * mm, "makeCopy" : false});
        }
        {
            var Q0;
            Q0=makeQuery(id+"F20.opExtrude","SWEPT_BODY",BODY,{"disambiguationData":[OSD([sQuery(id+"F19.wireOp",EDGE,"E104"),sQuery(id+"F19.wireOp",EDGE,"E105"),sQuery(id+"F19.wireOp",EDGE,"E106"),sQuery(id+"F19.wireOp",EDGE,"E107")])]});
            transform(context, id + "F36", {"entities" : qUnion([Q0]), "transformType" : TransformType.TRANSLATION_3D, "dx" : 101.6 * mm, "dy" : 0 * mm, "dz" : 0 * mm, "makeCopy" : false});
        }
    });
